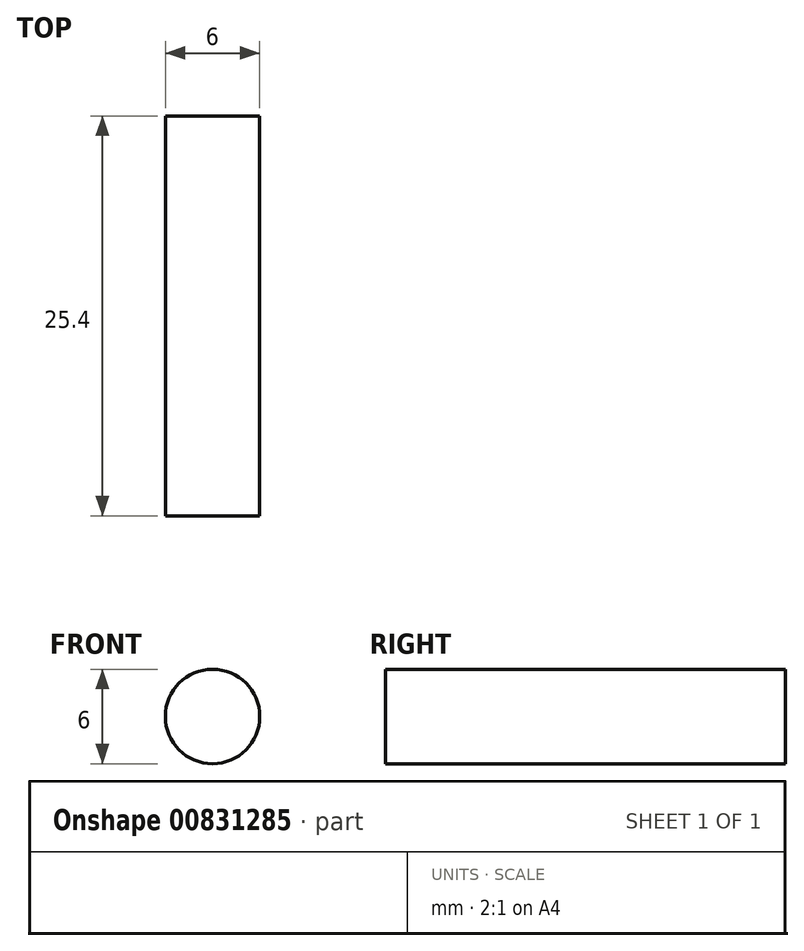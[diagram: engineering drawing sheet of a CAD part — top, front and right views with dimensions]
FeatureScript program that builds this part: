
annotation { "Feature Type Name" : "Feature", "Feature Type Description" : "" }
export const myFeature = defineFeature(function(context is Context, id is Id, definition is map)
    precondition{}
    {
        {
            var Q0;
            Q0=qCreatedBy(makeId("Front.planeOp"),FACE);
            var sketch = newSketch(context, id + "F0", { "sketchPlane" : qUnion([Q0])});
            skCircle(sketch, "E0", {"center": v(-52.27, 43.7) * mm, "radius": 3 * mm});
            skSolve(sketch);
        }
        {
            var Q0;
            Q0=makeQuery(id+"F0.imprint","IMPRINT",FACE,{"disambiguationData":[TD([[makeQuery(id+"F0.imprint","IMPRINT",EDGE,{"derivedFrom":sQuery(id+"F0.wireOp",EDGE,"E0")}),1.0]])]});
            extrude(context, id + "F1", {"entities" : qUnion([Q0]), "depth" : 25.4 * mm, "offsetDistance" : 25.4 * mm});
        }
    });
